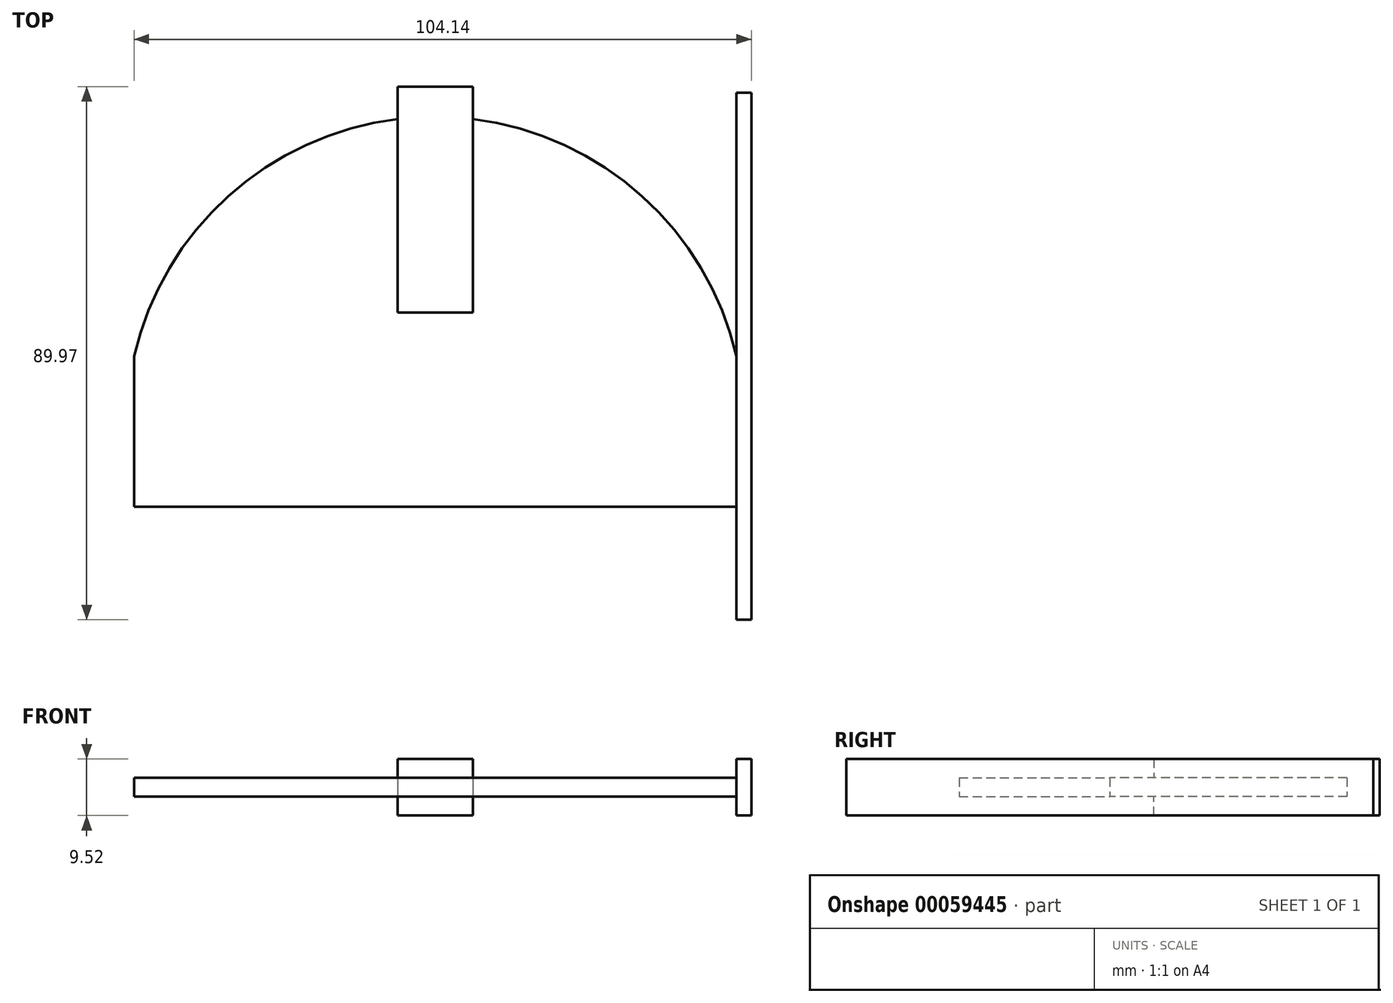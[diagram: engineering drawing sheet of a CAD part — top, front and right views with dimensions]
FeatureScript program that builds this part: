
annotation { "Feature Type Name" : "Feature", "Feature Type Description" : "" }
export const myFeature = defineFeature(function(context is Context, id is Id, definition is map)
    precondition{}
    {
        {
            var Q0;
            Q0=qCreatedBy(makeId("Top.planeOp"),FACE);
            var sketch = newSketch(context, id + "F0", { "sketchPlane" : qUnion([Q0])});
            skLineSegment(sketch, "E0", {"start": v(0, 0) * mm, "end": v(-50.8, 0) * mm});
            skLineSegment(sketch, "E1", {"start": v(0, 0) * mm, "end": v(50.8, 0) * mm});
            skLineSegment(sketch, "E2", {"start": v(-50.8, 0) * mm, "end": v(-50.8, 25.4) * mm});
            skLineSegment(sketch, "E3", {"start": v(50.8, 0) * mm, "end": v(50.8, 25.4) * mm});
            skArc(sketch, "E4", {"start": v(50.8, 25.4) * mm, "mid": v(0, 65.84) * mm, "end": v(-50.8, 25.4) * mm});
            skLineSegment(sketch, "E5", {"start": v(0, 70.92) * mm, "end": v(-6.35, 70.92) * mm});
            skLineSegment(sketch, "E6", {"start": v(0, 70.92) * mm, "end": v(6.35, 70.92) * mm});
            skLineSegment(sketch, "E7", {"start": v(0, 32.82) * mm, "end": v(-6.35, 32.82) * mm});
            skLineSegment(sketch, "E8", {"start": v(0, 32.82) * mm, "end": v(6.35, 32.82) * mm});
            skLineSegment(sketch, "E9", {"start": v(-6.35, 70.92) * mm, "end": v(-6.35, 32.82) * mm});
            skLineSegment(sketch, "E10", {"start": v(6.35, 70.92) * mm, "end": v(6.35, 32.82) * mm});
            skSolve(sketch);
        }
        {
            var Q0;
            Q0=makeQuery(id+"F0.imprint","IMPRINT",FACE,{"disambiguationData":[TD([[makeQuery(id+"F0.imprint","IMPRINT",EDGE,{"derivedFrom":sQuery(id+"F0.wireOp",EDGE,"E0")}),-1.0]])]});
            extrude(context, id + "F1", {"entities" : qUnion([Q0]), "depth" : 1.59 * mm});
        }
        {
            var Q0;
            Q0=makeQuery(id+"F1.opExtrude","CAP_FACE",FACE,{"disambiguationData":[OSD([sQuery(id+"F0.wireOp",EDGE,"E0"),sQuery(id+"F0.wireOp",EDGE,"E1"),sQuery(id+"F0.wireOp",EDGE,"E2"),sQuery(id+"F0.wireOp",EDGE,"E3"),sQuery(id+"F0.wireOp",EDGE,"E4"),sQuery(id+"F0.wireOp",EDGE,"E5"),sQuery(id+"F0.wireOp",EDGE,"E6"),sQuery(id+"F0.wireOp",EDGE,"E9"),sQuery(id+"F0.wireOp",EDGE,"E10")])],"isStart":true});
            extrude(context, id + "F2", {"entities" : qUnion([Q0]), "operationType" : NewBodyOperationType.ADD, "depth" : 1.59 * mm});
        }
        {
            var Q0;
            {var subQ1=sQuery(id+"F0.wireOp",EDGE,"E7");Q0=makeQuery(id+"F0.imprint","IMPRINT",FACE,{"disambiguationData":[TD([[makeQuery(id+"F0.imprint","IMPRINT",EDGE,{"derivedFrom":subQ1}),-1.0]])]});}
            var Q1;
            {var subQ1=sQuery(id+"F0.wireOp",EDGE,"E5");Q1=makeQuery(id+"F0.imprint","IMPRINT",FACE,{"disambiguationData":[TD([[makeQuery(id+"F0.imprint","IMPRINT",EDGE,{"derivedFrom":subQ1}),1.0]])]});}
            extrude(context, id + "F3", {"entities" : qUnion([Q0, Q1]), "operationType" : NewBodyOperationType.ADD, "depth" : 4.76 * mm});
        }
        {
            var Q0;
            {var subQ1=sQuery(id+"F0.wireOp",EDGE,"E7");Q0=makeQuery(id+"F0.imprint","IMPRINT",FACE,{"disambiguationData":[TD([[makeQuery(id+"F0.imprint","IMPRINT",EDGE,{"derivedFrom":subQ1}),-1.0]])]});}
            var Q1;
            {var subQ1=sQuery(id+"F0.wireOp",EDGE,"E5");Q1=makeQuery(id+"F0.imprint","IMPRINT",FACE,{"disambiguationData":[TD([[makeQuery(id+"F0.imprint","IMPRINT",EDGE,{"derivedFrom":subQ1}),1.0]])]});}
            extrude(context, id + "F4", {"entities" : qUnion([Q0, Q1]), "operationType" : NewBodyOperationType.ADD, "oppositeDirection" : true, "depth" : 4.76 * mm});
        }
        {
            var Q0;
            {var subQ0=sQuery(id+"F0.wireOp",EDGE,"E3");Q0=makeQuery(id+"F2.boolean.opBoolean","MERGE",FACE,{"derivedFrom":[makeQuery(id+"F1.opExtrude","SWEPT_FACE",FACE,{"disambiguationData":[OSD([subQ0])]}),makeQuery(id+"F2.opExtrude","SWEPT_FACE",FACE,{"disambiguationData":[OSD([subQ0])]})]});}
            var sketch = newSketch(context, id + "F5", { "sketchPlane" : qUnion([Q0])});
            skLineSegment(sketch, "E11", {"start": v(0, 1.59) * mm, "end": v(-19.05, 1.59) * mm});
            skLineSegment(sketch, "E12", {"start": v(0, -1.59) * mm, "end": v(-19.05, -1.59) * mm});
            skLineSegment(sketch, "E13", {"start": v(-19.05, 1.59) * mm, "end": v(-19.05, -1.59) * mm});
            skLineSegment(sketch, "E14", {"start": v(0, 1.59) * mm, "end": v(69.85, 1.59) * mm});
            skLineSegment(sketch, "E15", {"start": v(0, -1.59) * mm, "end": v(69.85, -1.59) * mm});
            skLineSegment(sketch, "E16", {"start": v(69.85, 1.59) * mm, "end": v(69.85, -1.59) * mm});
            skLineSegment(sketch, "E17", {"start": v(-19.05, 1.59) * mm, "end": v(-19.05, 4.76) * mm});
            skLineSegment(sketch, "E18", {"start": v(-19.05, -1.59) * mm, "end": v(-19.05, -4.76) * mm});
            skLineSegment(sketch, "E19", {"start": v(-19.05, 4.76) * mm, "end": v(69.85, 4.76) * mm});
            skLineSegment(sketch, "E20", {"start": v(-19.05, -4.76) * mm, "end": v(69.85, -4.76) * mm});
            skLineSegment(sketch, "E21", {"start": v(69.85, 4.76) * mm, "end": v(69.85, -4.76) * mm});
            skSolve(sketch);
        }
        {
            var Q0;
            {var subQ7=sQuery(id+"F5.wireOp",EDGE,"E11");Q0=makeQuery(id+"F5.imprint","IMPRINT",FACE,{"disambiguationData":[TD([[makeQuery(id+"F5.imprint","IMPRINT",EDGE,{"derivedFrom":subQ7}),-1.0]])]});}
            var Q1;
            {var subQ1=sQuery(id+"F0.wireOp",EDGE,"E3");var subQ2=sQuery(id+"F0.wireOp",EDGE,"E1");var subQ3=makeQuery(id+"F2.boolean.opBoolean","MERGE",EDGE,{"derivedFrom":[makeQuery(id+"F1.opExtrude","SWEPT_EDGE",EDGE,{"disambiguationData":[OSD([subQ2,subQ1])]}),makeQuery(id+"F2.opExtrude","SWEPT_EDGE",EDGE,{"disambiguationData":[OSD([subQ2,subQ1])]})]});Q1=makeQuery(id+"F5.imprint","IMPRINT",FACE,{"disambiguationData":[TD([[makeQuery(id+"F5.imprint","IMPRINT",EDGE,{"derivedFrom":subQ3}),1.0]])]});}
            var Q2;
            Q2=makeQuery(id+"F5.imprint","IMPRINT",FACE,{"disambiguationData":[TD([[makeQuery(id+"F5.imprint","IMPRINT",EDGE,{"derivedFrom":sQuery(id+"F5.wireOp",EDGE,"E11")}),1.0]])]});
            var Q3;
            {var subQ0=sQuery(id+"F5.wireOp",EDGE,"E12");Q3=makeQuery(id+"F5.imprint","IMPRINT",FACE,{"disambiguationData":[TD([[makeQuery(id+"F5.imprint","IMPRINT",EDGE,{"derivedFrom":subQ0}),1.0]])]});}
            var Q4;
            {var subQ1=sQuery(id+"F0.wireOp",EDGE,"E4");var subQ2=sQuery(id+"F0.wireOp",EDGE,"E3");var subQ3=makeQuery(id+"F2.boolean.opBoolean","MERGE",EDGE,{"derivedFrom":[makeQuery(id+"F1.opExtrude","SWEPT_EDGE",EDGE,{"disambiguationData":[OSD([subQ2,subQ1])]}),makeQuery(id+"F2.opExtrude","SWEPT_EDGE",EDGE,{"disambiguationData":[OSD([subQ2,subQ1])]})]});Q4=makeQuery(id+"F5.imprint","IMPRINT",FACE,{"disambiguationData":[TD([[makeQuery(id+"F5.imprint","IMPRINT",EDGE,{"derivedFrom":subQ3}),1.0]])]});}
            extrude(context, id + "F6", {"entities" : qUnion([Q0, Q1, Q2, Q3, Q4]), "operationType" : NewBodyOperationType.ADD, "depth" : 2.54 * mm});
        }
    });
